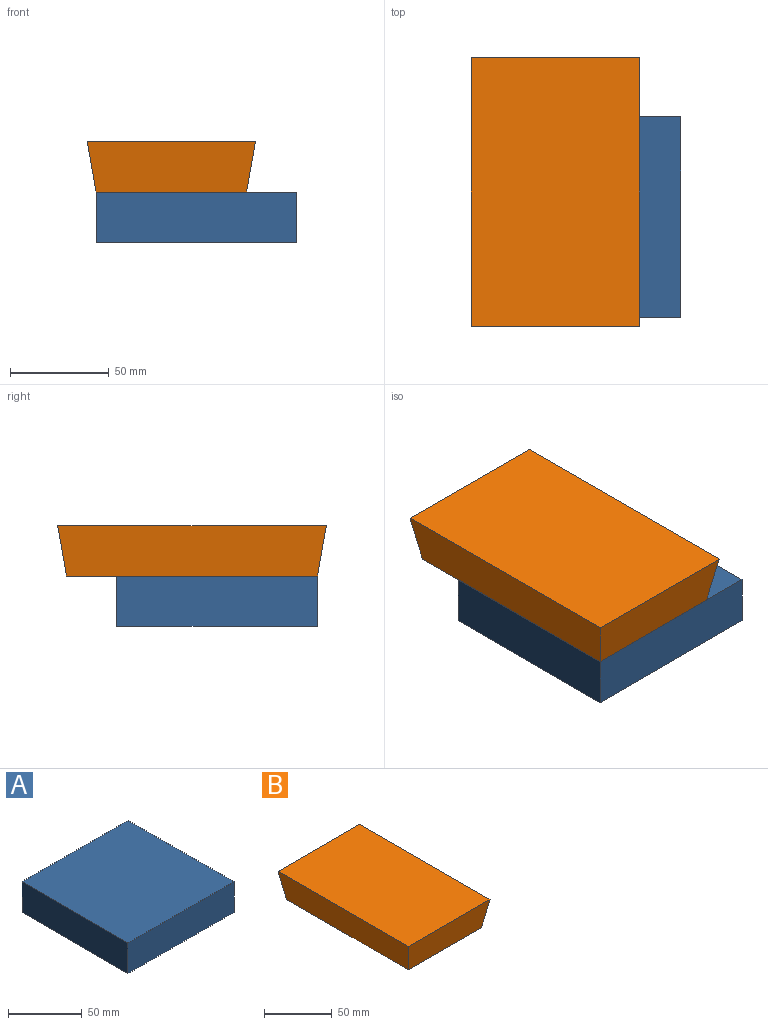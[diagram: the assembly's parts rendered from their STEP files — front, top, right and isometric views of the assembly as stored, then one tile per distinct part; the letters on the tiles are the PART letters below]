
ASSEMBLY  parts=2 mates=1
PART A: 12 faces, bbox 101.6x101.6x25.4 mm
  f0: plane 101.6x25.4mm, normal (-1,0,0), area 2580.6mm2, adj f1,f3,f4,f5
  f1: plane 101.6x25.4mm, normal (0,-1,0), area 2580.6mm2, adj f0,f2,f4,f5
  f2: plane 101.6x25.4mm, normal (1,0,0), area 2580.6mm2, adj f1,f3,f4,f5
  f3: plane 101.6x25.4mm, normal (0,1,0), area 2580.6mm2, adj f0,f2,f4,f5
  f4: plane 101.6x101.6mm, normal (0,0,1), area 10322.6mm2, adj f0,f1,f2,f3
  f5: plane 101.6x101.6mm, normal (0,0,-1), area 10322.6mm2, adj f0,f1,f2,f3
  f6: plane 96.52x20.32mm, normal (1,0,0), area 1961.3mm2, adj f7,f9,f10,f11
  f7: plane 96.52x20.32mm, normal (0,1,0), area 1961.3mm2, adj f6,f8,f10,f11
  f8: plane 96.52x20.32mm, normal (-1,0,0), area 1961.3mm2, adj f7,f9,f10,f11
  f9: plane 96.52x20.32mm, normal (0,-1,0), area 1961.3mm2, adj f6,f8,f10,f11
  f10: plane 96.52x96.52mm, normal (0,0,-1), area 9316.1mm2, adj f6,f7,f8,f9
  f11: plane 96.52x96.52mm, normal (0,0,1), area 9316.1mm2, adj f6,f7,f8,f9
PART B: 6 faces, bbox 85.2x136x25.4 mm
  f0: plane 85.16x25.4mm, normal (0,-0.98,-0.17), area 2080.9mm2, adj f1,f3,f4,f5
  f1: plane 135.96x25.4mm, normal (0.98,0,-0.17), area 3391.1mm2, adj f0,f2,f4,f5
  f2: plane 85.16x25.4mm, normal (0,0.98,-0.17), area 2080.9mm2, adj f1,f3,f4,f5
  f3: plane 135.96x25.4mm, normal (-0.98,0,-0.17), area 3391.1mm2, adj f0,f2,f4,f5
  f4: plane 135.96x85.16mm, normal (0,0,1), area 11577.8mm2, adj f0,f1,f2,f3
  f5: plane 127x76.2mm, normal (0,0,-1), area 9677.4mm2, adj f0,f1,f2,f3
PLACE A t=(-53.43,77.41,0)mm
PLACE B t=(-66.13,90.11,25.4)mm
MATE fastened A.f4 <-> B.f5  axis (0,0,1) through (-104.23,26.61,25.4)mm
